annotation { "Feature Type Name" : "Feature", "Feature Type Description" : "" }
export const myFeature = defineFeature(function(context is Context, id is Id, definition is map)
    precondition{}
    {
        {
            assignVariable(context, id + "F0", {"name" : "thickness", "anyValue" : 1.5});
        }
        {
            assignVariable(context, id + "F1", {"name" : "c_pcb_under", "anyValue" : 5.25});
        }
        {
            assignVariable(context, id + "F2", {"name" : "c_pcb_above", "anyValue" : 14.5});
        }
        {
            assignVariable(context, id + "F3", {"name" : "pcb", "anyValue" : 1.62});
        }
        {
            assignVariable(context, id + "F4", {"name" : "inside_height", "anyValue" : getVariable(context, 'c_pcb_under') + getVariable(context, 'pcb') + getVariable(context, 'c_pcb_above')});
        }
        {
            var Q0;
            Q0=qCreatedBy(makeId("Top.planeOp"),FACE);
            var sketch = newSketch(context, id + "F5", { "sketchPlane" : qUnion([Q0])});
            skLineSegment(sketch, "E0.bottom", {"start": v(50, 40.13) * mm, "end": v(-50, 40.13) * mm});
            skLineSegment(sketch, "E0.top", {"start": v(50, -40.13) * mm, "end": v(42.5, -40.13) * mm});
            skLineSegment(sketch, "E0.left", {"start": v(50, 40.12) * mm, "end": v(50, -40.13) * mm});
            skLineSegment(sketch, "E0.right", {"start": v(-50, 40.12) * mm, "end": v(-50, -40.13) * mm});
            skPoint(sketch, "E0.middle", {"position": v(0, 0) * mm});
            skLineSegment(sketch, "E1.bottom", {"start": v(-40, 40.13) * mm, "end": v(-31, 40.13) * mm});
            skLineSegment(sketch, "E1.top", {"start": v(-40, 34.62) * mm, "end": v(-31, 34.62) * mm});
            skLineSegment(sketch, "E1.left", {"start": v(-40, 40.12) * mm, "end": v(-40, 34.62) * mm});
            skLineSegment(sketch, "E1.right", {"start": v(-31, 40.12) * mm, "end": v(-31, 34.62) * mm});
            skCircle(sketch, "E2", {"center": v(-46, 36.13) * mm, "radius": 1.65 * mm});
            skCircle(sketch, "E3", {"center": v(46, 36.13) * mm, "radius": 1.65 * mm});
            skCircle(sketch, "E4", {"center": v(46, -36.13) * mm, "radius": 1.65 * mm});
            skCircle(sketch, "E5", {"center": v(-46, -36.13) * mm, "radius": 1.65 * mm});
            skLineSegment(sketch, "E6.bottom", {"start": v(-42.5, -40.13) * mm, "end": v(-26.5, -40.13) * mm});
            skLineSegment(sketch, "E6.top", {"start": v(-42.5, -18.77) * mm, "end": v(-26.5, -18.77) * mm});
            skLineSegment(sketch, "E6.left", {"start": v(-42.5, -40.13) * mm, "end": v(-42.5, -18.77) * mm});
            skLineSegment(sketch, "E6.right", {"start": v(-26.5, -40.13) * mm, "end": v(-26.5, -18.77) * mm});
            skLineSegment(sketch, "E7.bottom", {"start": v(-19.5, -40.13) * mm, "end": v(-3.5, -40.13) * mm});
            skLineSegment(sketch, "E7.top", {"start": v(-19.5, -18.77) * mm, "end": v(-3.5, -18.77) * mm});
            skLineSegment(sketch, "E7.left", {"start": v(-19.5, -40.13) * mm, "end": v(-19.5, -18.77) * mm});
            skLineSegment(sketch, "E7.right", {"start": v(-3.5, -40.13) * mm, "end": v(-3.5, -18.77) * mm});
            skLineSegment(sketch, "E8.bottom", {"start": v(3.5, -40.13) * mm, "end": v(19.5, -40.13) * mm});
            skLineSegment(sketch, "E8.top", {"start": v(3.5, -18.77) * mm, "end": v(19.5, -18.77) * mm});
            skLineSegment(sketch, "E8.left", {"start": v(3.5, -40.13) * mm, "end": v(3.5, -18.77) * mm});
            skLineSegment(sketch, "E8.right", {"start": v(19.5, -40.13) * mm, "end": v(19.5, -18.77) * mm});
            skLineSegment(sketch, "E9.bottom", {"start": v(26.5, -40.13) * mm, "end": v(42.5, -40.13) * mm});
            skLineSegment(sketch, "E9.top", {"start": v(26.5, -18.77) * mm, "end": v(42.5, -18.77) * mm});
            skLineSegment(sketch, "E9.left", {"start": v(26.5, -40.13) * mm, "end": v(26.5, -18.77) * mm});
            skLineSegment(sketch, "E9.right", {"start": v(42.5, -40.13) * mm, "end": v(42.5, -18.77) * mm});
            skLineSegment(sketch, "E10", {"start": v(-42.5, -40.13) * mm, "end": v(-50, -40.13) * mm});
            skLineSegment(sketch, "E11", {"start": v(-26.5, -40.13) * mm, "end": v(-42.5, -40.13) * mm});
            skLineSegment(sketch, "E12", {"start": v(-19.5, -40.13) * mm, "end": v(-26.5, -40.13) * mm});
            skLineSegment(sketch, "E13", {"start": v(-3.5, -40.13) * mm, "end": v(-19.5, -40.13) * mm});
            skLineSegment(sketch, "E14", {"start": v(3.5, -40.13) * mm, "end": v(-3.5, -40.13) * mm});
            skLineSegment(sketch, "E15", {"start": v(19.5, -40.13) * mm, "end": v(3.5, -40.13) * mm});
            skLineSegment(sketch, "E16", {"start": v(26.5, -40.13) * mm, "end": v(19.5, -40.13) * mm});
            skLineSegment(sketch, "E17", {"start": v(42.5, -40.13) * mm, "end": v(26.5, -40.13) * mm});
            skPoint(sketch, "E18", {"position": v(0, -40.13) * mm});
            skSolve(sketch);
        }
        {
            var Q0;
            Q0=qCreatedBy(makeId("Top.planeOp"),FACE);
            var sketch = newSketch(context, id + "F6", { "sketchPlane" : qUnion([Q0])});
            skLineSegment(sketch, "E19.bottom", {"start": v(51, 41.13) * mm, "end": v(-51, 41.13) * mm});
            skLineSegment(sketch, "E19.top", {"start": v(51, -41.13) * mm, "end": v(-51, -41.13) * mm});
            skLineSegment(sketch, "E19.left", {"start": v(51, 41.13) * mm, "end": v(51, -41.13) * mm});
            skLineSegment(sketch, "E19.right", {"start": v(-51, 41.13) * mm, "end": v(-51, -41.13) * mm});
            skPoint(sketch, "E19.middle", {"position": v(0, 0) * mm});
            skLineSegment(sketch, "E20.bottom", {"start": v(52.5, 42.63) * mm, "end": v(-52.5, 42.63) * mm});
            skLineSegment(sketch, "E20.top", {"start": v(52.5, -42.63) * mm, "end": v(-52.5, -42.63) * mm});
            skLineSegment(sketch, "E20.left", {"start": v(52.5, 42.63) * mm, "end": v(52.5, -42.63) * mm});
            skLineSegment(sketch, "E20.right", {"start": v(-52.5, 42.63) * mm, "end": v(-52.5, -42.63) * mm});
            skLineSegment(sketch, "E21.bottom", {"start": v(28.33, 41.13) * mm, "end": v(41.83, 41.13) * mm});
            skLineSegment(sketch, "E21.top", {"start": v(28.33, 25.63) * mm, "end": v(41.83, 25.63) * mm});
            skLineSegment(sketch, "E21.left", {"start": v(28.33, 41.13) * mm, "end": v(28.33, 25.63) * mm});
            skLineSegment(sketch, "E21.right", {"start": v(41.83, 41.13) * mm, "end": v(41.83, 25.63) * mm});
            skLineSegment(sketch, "E22.bottom", {"start": v(29.83, 41.13) * mm, "end": v(40.33, 41.13) * mm});
            skLineSegment(sketch, "E22.top", {"start": v(29.83, 27.13) * mm, "end": v(40.33, 27.13) * mm});
            skLineSegment(sketch, "E22.left", {"start": v(29.83, 41.13) * mm, "end": v(29.83, 27.13) * mm});
            skLineSegment(sketch, "E22.right", {"start": v(40.33, 41.13) * mm, "end": v(40.33, 27.13) * mm});
            skPoint(sketch, "E23", {"position": v(35.08, 27.13) * mm});
            skLineSegment(sketch, "E24.bottom", {"start": v(-51, 41.13) * mm, "end": v(-43.25, 41.13) * mm});
            skLineSegment(sketch, "E24.top", {"start": v(-51, 33.37) * mm, "end": v(-45.75, 33.37) * mm});
            skLineSegment(sketch, "E24.left", {"start": v(-51, 41.13) * mm, "end": v(-51, 33.37) * mm});
            skLineSegment(sketch, "E24.right", {"start": v(-43.25, 41.13) * mm, "end": v(-43.25, 35.88) * mm});
            skLineSegment(sketch, "E25.bottom", {"start": v(51, 41.13) * mm, "end": v(43.25, 41.13) * mm});
            skLineSegment(sketch, "E25.top", {"start": v(51, 33.37) * mm, "end": v(45.75, 33.37) * mm});
            skLineSegment(sketch, "E25.left", {"start": v(51, 41.13) * mm, "end": v(51, 33.37) * mm});
            skLineSegment(sketch, "E25.right", {"start": v(43.25, 41.12) * mm, "end": v(43.25, 35.88) * mm});
            skLineSegment(sketch, "E26.bottom", {"start": v(51, -41.13) * mm, "end": v(43.25, -41.13) * mm});
            skLineSegment(sketch, "E26.top", {"start": v(51, -33.38) * mm, "end": v(45.75, -33.38) * mm});
            skLineSegment(sketch, "E26.left", {"start": v(51, -41.13) * mm, "end": v(51, -33.38) * mm});
            skLineSegment(sketch, "E26.right", {"start": v(43.25, -41.13) * mm, "end": v(43.25, -35.88) * mm});
            skLineSegment(sketch, "E27.bottom", {"start": v(-51, -41.13) * mm, "end": v(-43.25, -41.13) * mm});
            skLineSegment(sketch, "E27.top", {"start": v(-51, -33.38) * mm, "end": v(-45.75, -33.38) * mm});
            skLineSegment(sketch, "E27.left", {"start": v(-51, -41.13) * mm, "end": v(-51, -33.38) * mm});
            skLineSegment(sketch, "E27.right", {"start": v(-43.25, -41.13) * mm, "end": v(-43.25, -35.88) * mm});
            skPoint(sketch, "E28.visualSharp", {"position": v(-43.25, 33.37) * mm});
            skArc(sketch, "E28.filletArc", {"start": v(-45.75, 33.37) * mm, "mid": v(-43.98, 34.1) * mm, "end": v(-43.25, 35.88) * mm});
            skPoint(sketch, "E29.visualSharp", {"position": v(43.25, 33.37) * mm});
            skArc(sketch, "E29.filletArc", {"start": v(43.25, 35.88) * mm, "mid": v(43.98, 34.1) * mm, "end": v(45.75, 33.37) * mm});
            skPoint(sketch, "E30.visualSharp", {"position": v(43.25, -33.38) * mm});
            skArc(sketch, "E30.filletArc", {"start": v(45.75, -33.38) * mm, "mid": v(43.98, -34.1) * mm, "end": v(43.25, -35.88) * mm});
            skPoint(sketch, "E31.visualSharp", {"position": v(-43.25, -33.38) * mm});
            skArc(sketch, "E31.filletArc", {"start": v(-43.25, -35.88) * mm, "mid": v(-43.98, -34.1) * mm, "end": v(-45.75, -33.38) * mm});
            skSolve(sketch);
        }
        {
            var Q0;
            Q0=qCreatedBy(makeId("Front.planeOp"),FACE);
            var sketch = newSketch(context, id + "F7", { "sketchPlane" : qUnion([Q0])});
            skLineSegment(sketch, "E32.bottom", {"start": v(52.5, -24.37) * mm, "end": v(-52.5, -24.37) * mm});
            skLineSegment(sketch, "E32.top", {"start": v(52.5, 0) * mm, "end": v(-52.5, 0) * mm});
            skLineSegment(sketch, "E32.left", {"start": v(52.5, -24.37) * mm, "end": v(52.5, 0) * mm});
            skLineSegment(sketch, "E32.right", {"start": v(-52.5, -24.37) * mm, "end": v(-52.5, 0) * mm});
            skPoint(sketch, "E32.middle", {"position": v(0, -12.19) * mm});
            skLineSegment(sketch, "E33.bottom", {"start": v(-42.5, -16) * mm, "end": v(-26.5, -16) * mm});
            skLineSegment(sketch, "E33.top", {"start": v(-42.5, -3.5) * mm, "end": v(-26.5, -3.5) * mm});
            skLineSegment(sketch, "E33.left", {"start": v(-42.5, -16) * mm, "end": v(-42.5, -3.5) * mm});
            skLineSegment(sketch, "E33.right", {"start": v(-26.5, -16) * mm, "end": v(-26.5, -3.5) * mm});
            skLineSegment(sketch, "E34.bottom", {"start": v(-19.5, -16) * mm, "end": v(-3.5, -16) * mm});
            skLineSegment(sketch, "E34.top", {"start": v(-19.5, -3.5) * mm, "end": v(-3.5, -3.5) * mm});
            skLineSegment(sketch, "E34.left", {"start": v(-19.5, -16) * mm, "end": v(-19.5, -3.5) * mm});
            skLineSegment(sketch, "E34.right", {"start": v(-3.5, -16) * mm, "end": v(-3.5, -3.5) * mm});
            skLineSegment(sketch, "E35.bottom", {"start": v(3.5, -16) * mm, "end": v(19.5, -16) * mm});
            skLineSegment(sketch, "E35.top", {"start": v(3.5, -3.5) * mm, "end": v(19.5, -3.5) * mm});
            skLineSegment(sketch, "E35.left", {"start": v(3.5, -16) * mm, "end": v(3.5, -3.5) * mm});
            skLineSegment(sketch, "E35.right", {"start": v(19.5, -16) * mm, "end": v(19.5, -3.5) * mm});
            skLineSegment(sketch, "E36.bottom", {"start": v(26.5, -16) * mm, "end": v(42.5, -16) * mm});
            skLineSegment(sketch, "E36.top", {"start": v(26.5, -3.5) * mm, "end": v(42.5, -3.5) * mm});
            skLineSegment(sketch, "E36.left", {"start": v(26.5, -16) * mm, "end": v(26.5, -3.5) * mm});
            skLineSegment(sketch, "E36.right", {"start": v(42.5, -16) * mm, "end": v(42.5, -3.5) * mm});
            skSolve(sketch);
        }
        {
            var Q0;
            Q0 = qSketchRegion(id + "F6", true);
            var Q1;
            Q1=makeQuery(id+"F6.imprint","IMPRINT",FACE,{"disambiguationData":[TD([[makeQuery(id+"F6.imprint","IMPRINT",EDGE,{"derivedFrom":sQuery(id+"F6.wireOp",EDGE,"E24.bottom")}),-1.0]])]});
            var Q2;
            Q2=makeQuery(id+"F6.imprint","IMPRINT",FACE,{"disambiguationData":[TD([[makeQuery(id+"F6.imprint","IMPRINT",EDGE,{"derivedFrom":sQuery(id+"F6.wireOp",EDGE,"E27.bottom")}),1.0]])]});
            var Q3;
            Q3=makeQuery(id+"F6.imprint","IMPRINT",FACE,{"disambiguationData":[TD([[makeQuery(id+"F6.imprint","IMPRINT",EDGE,{"derivedFrom":sQuery(id+"F6.wireOp",EDGE,"E26.bottom")}),-1.0]])]});
            var Q4;
            Q4=makeQuery(id+"F6.imprint","IMPRINT",FACE,{"disambiguationData":[TD([[makeQuery(id+"F6.imprint","IMPRINT",EDGE,{"derivedFrom":sQuery(id+"F6.wireOp",EDGE,"E25.bottom")}),1.0]])]});
            var Q5;
            Q5=sQuery(id+"F7.wireOp",VERTEX,"E32.left.start");
            extrude(context, id + "F8", {"entities" : qUnion([Q0, Q1, Q2, Q3, Q4]), "endBound" : BoundingType.UP_TO_VERTEX, "oppositeDirection" : true, "endBoundEntityVertex" : qUnion([Q5]), "depth" : (2 * getVariable(context, 'thickness') + getVariable(context, 'inside_height')) * mm});
        }
        {
            var Q0;
            Q0=makeQuery(id+"F6.imprint","IMPRINT",FACE,{"disambiguationData":[TD([[makeQuery(id+"F6.imprint","IMPRINT",EDGE,{"derivedFrom":sQuery(id+"F6.wireOp",EDGE,"E22.bottom")}),-1.0]])]});
            var Q1;
            Q1=makeQuery(id+"F6.imprint","IMPRINT",FACE,{"disambiguationData":[TD([[makeQuery(id+"F6.imprint","IMPRINT",EDGE,{"derivedFrom":sQuery(id+"F6.wireOp",EDGE,"E21.top")}),1.0]])]});
            var Q2;
            Q2=makeQuery(id+"F6.imprint","IMPRINT",FACE,{"disambiguationData":[TD([[makeQuery(id+"F6.imprint","IMPRINT",EDGE,{"derivedFrom":sQuery(id+"F6.wireOp",EDGE,"E19.top")}),-1.0]])]});
            extrude(context, id + "F9", {"entities" : qUnion([Q0, Q1, Q2]), "operationType" : NewBodyOperationType.ADD, "oppositeDirection" : true, "depth" : (getVariable(context, 'thickness')) * mm});
        }
        {
            var Q0;
            Q0=qCreatedBy(makeId("Top.planeOp"),FACE);
            var sketch = newSketch(context, id + "F10", { "sketchPlane" : qUnion([Q0])});
            skPoint(sketch, "E37.middle", {"position": v(0, 0) * mm});
            skText(sketch, "E38", { "text": "Northbound Networks\n", "fontName": "OpenSans-Bold.ttf"});
            skText(sketch, "E39", { "text": "Zodiac FX", "fontName": "OpenSans-Bold.ttf"});
            const initialGuessF10  = {"E38": [-0.045, 0.005, 1, 0, 0.00571], "E39": [-0.02996, -0.014, 1, 0, 0.009]};
            skSetInitialGuess(sketch, initialGuessF10);
            skSolve(sketch);
        }
        {
            var Q0;
            Q0 = qSketchRegion(id + "F10", true);
            extrude(context, id + "F11", {"entities" : qUnion([Q0]), "operationType" : NewBodyOperationType.REMOVE, "oppositeDirection" : true, "depth" : .5 * mm});
        }
        {
            var Q0;
            Q0=makeQuery(id+"F6.imprint","IMPRINT",FACE,{"disambiguationData":[TD([[makeQuery(id+"F6.imprint","IMPRINT",EDGE,{"derivedFrom":sQuery(id+"F6.wireOp",EDGE,"E21.top")}),1.0]])]});
            extrude(context, id + "F12", {"entities" : qUnion([Q0]), "operationType" : NewBodyOperationType.ADD, "oppositeDirection" : true, "depth" : (getVariable(context, 'thickness') + 12) * mm});
        }
        {
            var Q0;
            Q0=makeQuery(id+"F7.imprint","IMPRINT",FACE,{"disambiguationData":[TD([[makeQuery(id+"F7.imprint","IMPRINT",EDGE,{"derivedFrom":sQuery(id+"F7.wireOp",EDGE,"E33.bottom")}),1.0]])]});
            var Q1;
            Q1=makeQuery(id+"F7.imprint","IMPRINT",FACE,{"disambiguationData":[TD([[makeQuery(id+"F7.imprint","IMPRINT",EDGE,{"derivedFrom":sQuery(id+"F7.wireOp",EDGE,"E34.bottom")}),1.0]])]});
            var Q2;
            Q2=makeQuery(id+"F7.imprint","IMPRINT",FACE,{"disambiguationData":[TD([[makeQuery(id+"F7.imprint","IMPRINT",EDGE,{"derivedFrom":sQuery(id+"F7.wireOp",EDGE,"E36.bottom")}),1.0]])]});
            var Q3;
            Q3=makeQuery(id+"F7.imprint","IMPRINT",FACE,{"disambiguationData":[TD([[makeQuery(id+"F7.imprint","IMPRINT",EDGE,{"derivedFrom":sQuery(id+"F7.wireOp",EDGE,"E35.bottom")}),1.0]])]});
            var Q4;
            Q4=makeQuery(id+"F8.opExtrude","SWEPT_FACE",FACE,{"disambiguationData":[OSD([sQuery(id+"F6.wireOp",EDGE,"E20.top")])]});
            extrude(context, id + "F13", {"entities" : qUnion([Q0, Q1, Q2, Q3]), "operationType" : NewBodyOperationType.REMOVE, "endBound" : BoundingType.UP_TO_SURFACE, "endBoundEntityFace" : qUnion([Q4]), "depth" : 25 * mm});
        }
        {
            var Q0;
            Q0=qCreatedBy(makeId("Front.planeOp"),FACE);
            var sketch = newSketch(context, id + "F14", { "sketchPlane" : qUnion([Q0])});
            skCircle(sketch, "E40", {"center": v(35.08, -8) * mm, "radius": 3.25 * mm});
            skLineSegment(sketch, "E41.bottom", {"start": v(-31, -12.5) * mm, "end": v(-40, -12.5) * mm});
            skLineSegment(sketch, "E41.top", {"start": v(-31, -16) * mm, "end": v(-40, -16) * mm});
            skLineSegment(sketch, "E41.left", {"start": v(-31, -12.5) * mm, "end": v(-31, -16) * mm});
            skLineSegment(sketch, "E41.right", {"start": v(-40, -12.5) * mm, "end": v(-40, -16) * mm});
            skCircle(sketch, "E42", {"center": v(35.08, -8) * mm, "radius": 2 * mm});
            skSolve(sketch);
        }
        {
            var Q0;
            Q0=makeQuery(id+"F14.imprint","IMPRINT",FACE,{"disambiguationData":[TD([[makeQuery(id+"F14.imprint","IMPRINT",EDGE,{"derivedFrom":sQuery(id+"F14.wireOp",EDGE,"E42")}),1.0]])]});
            var Q1;
            Q1=makeQuery(id+"F8.opExtrude","SWEPT_FACE",FACE,{"disambiguationData":[OSD([sQuery(id+"F6.wireOp",EDGE,"E20.bottom")])]});
            extrude(context, id + "F15", {"entities" : qUnion([Q0]), "operationType" : NewBodyOperationType.REMOVE, "endBound" : BoundingType.UP_TO_SURFACE, "oppositeDirection" : true, "endBoundEntityFace" : qUnion([Q1]), "depth" : 25 * mm});
        }
        {
            var Q0;
            Q0=makeQuery(id+"F14.imprint","IMPRINT",FACE,{"disambiguationData":[TD([[makeQuery(id+"F14.imprint","IMPRINT",EDGE,{"derivedFrom":sQuery(id+"F14.wireOp",EDGE,"E40")}),1.0]])]});
            var Q1;
            Q1=makeQuery(id+"F12.opExtrude","SWEPT_FACE",FACE,{"disambiguationData":[OSD([sQuery(id+"F6.wireOp",EDGE,"E22.top")])]});
            extrude(context, id + "F16", {"entities" : qUnion([Q0]), "operationType" : NewBodyOperationType.REMOVE, "endBound" : BoundingType.UP_TO_SURFACE, "oppositeDirection" : true, "endBoundEntityFace" : qUnion([Q1]), "depth" : 25 * mm});
        }
        {
            var Q0;
            Q0=makeQuery(id+"F14.imprint","IMPRINT",FACE,{"disambiguationData":[TD([[makeQuery(id+"F14.imprint","IMPRINT",EDGE,{"derivedFrom":sQuery(id+"F14.wireOp",EDGE,"E41.bottom")}),1.0]])]});
            var Q1;
            Q1=makeQuery(id+"F8.opExtrude","SWEPT_FACE",FACE,{"disambiguationData":[OSD([sQuery(id+"F6.wireOp",EDGE,"E20.bottom")])]});
            extrude(context, id + "F17", {"entities" : qUnion([Q0]), "operationType" : NewBodyOperationType.REMOVE, "endBound" : BoundingType.UP_TO_SURFACE, "oppositeDirection" : true, "endBoundEntityFace" : qUnion([Q1]), "depth" : 25 * mm});
        }
    });